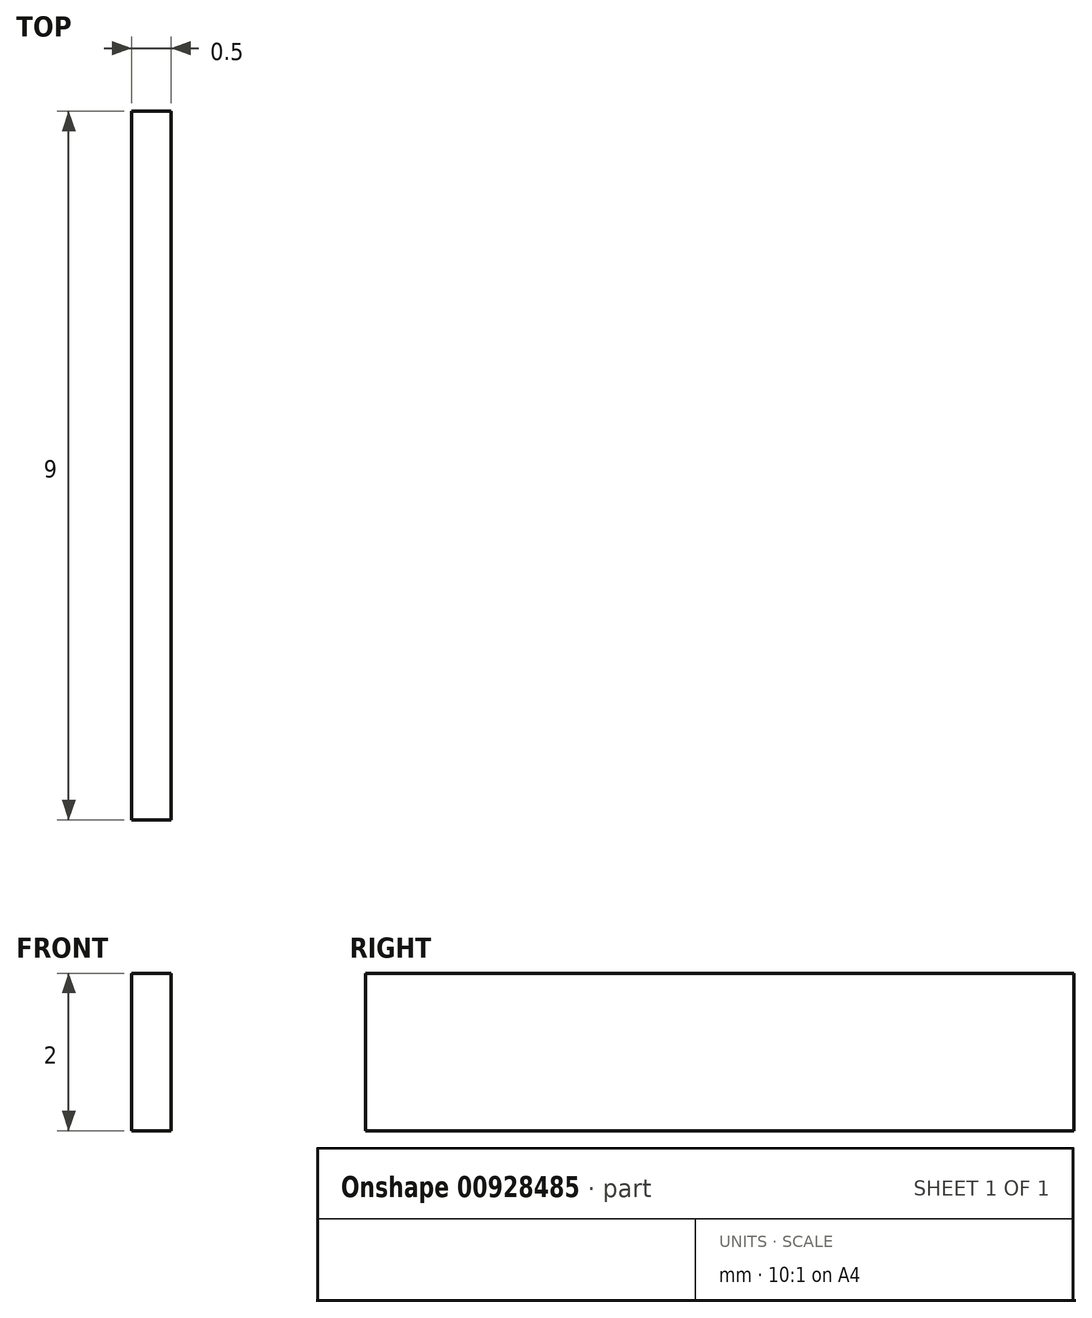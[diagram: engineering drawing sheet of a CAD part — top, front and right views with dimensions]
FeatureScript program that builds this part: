
annotation { "Feature Type Name" : "Feature", "Feature Type Description" : "" }
export const myFeature = defineFeature(function(context is Context, id is Id, definition is map)
    precondition{}
    {
        {
            var Q0;
            Q0=qCreatedBy(makeId("Right.planeOp"),FACE);
            var sketch = newSketch(context, id + "F0", { "sketchPlane" : qUnion([Q0])});
            skLineSegment(sketch, "E0.bottom", {"start": v(4.5, 1) * mm, "end": v(-4.5, 1) * mm});
            skLineSegment(sketch, "E0.top", {"start": v(4.5, -1) * mm, "end": v(-4.5, -1) * mm});
            skLineSegment(sketch, "E0.left", {"start": v(4.5, 1) * mm, "end": v(4.5, -1) * mm});
            skLineSegment(sketch, "E0.right", {"start": v(-4.5, 1) * mm, "end": v(-4.5, -1) * mm});
            skPoint(sketch, "E0.middle", {"position": v(0, 0) * mm});
            skSolve(sketch);
        }
        {
            var Q0;
            Q0=makeQuery(id+"F0.imprint","IMPRINT",FACE,{"disambiguationData":[TD([[makeQuery(id+"F0.imprint","IMPRINT",EDGE,{"derivedFrom":sQuery(id+"F0.wireOp",EDGE,"E0.bottom")}),1.0]])]});
            extrude(context, id + "F1", {"entities" : qUnion([Q0]), "depth" : 0.5 * mm, "offsetDistance" : 25 * mm});
        }
    });
